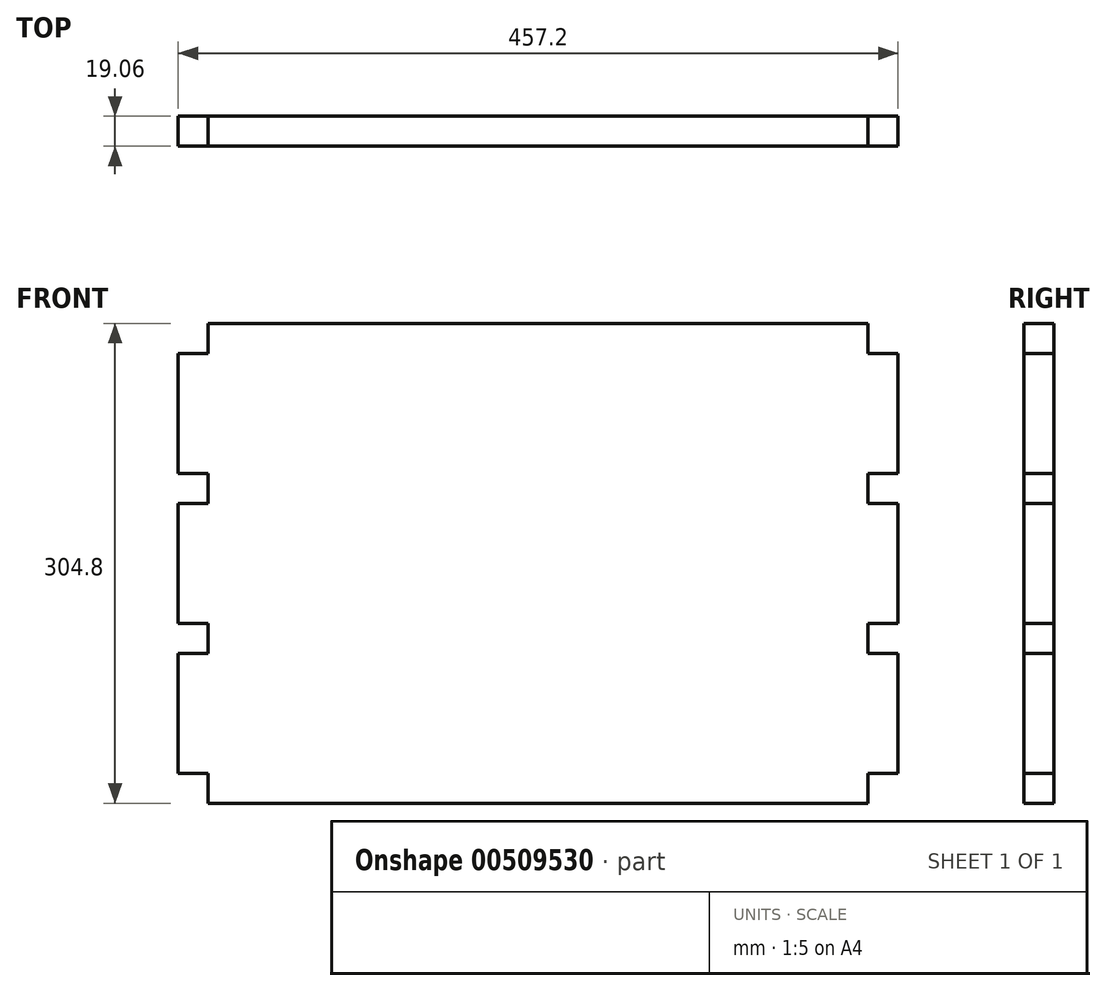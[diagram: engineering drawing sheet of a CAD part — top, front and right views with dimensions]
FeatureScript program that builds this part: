
annotation { "Feature Type Name" : "Feature", "Feature Type Description" : "" }
export const myFeature = defineFeature(function(context is Context, id is Id, definition is map)
    precondition{}
    {
        {
            var Q0;
            Q0=qCreatedBy(makeId("Front.planeOp"),FACE);
            var sketch = newSketch(context, id + "F0", { "sketchPlane" : qUnion([Q0])});
            skLineSegment(sketch, "E0.bottom", {"start": v(-228.6, 152.4) * mm, "end": v(228.6, 152.4) * mm});
            skLineSegment(sketch, "E0.top", {"start": v(-228.6, -152.4) * mm, "end": v(228.6, -152.4) * mm});
            skLineSegment(sketch, "E0.left", {"start": v(-228.6, 152.4) * mm, "end": v(-228.6, -152.4) * mm});
            skLineSegment(sketch, "E0.right", {"start": v(228.6, 152.4) * mm, "end": v(228.6, -152.4) * mm});
            skPoint(sketch, "E0.middle", {"position": v(0, 0) * mm});
            skSolve(sketch);
        }
        {
            var Q0;
            Q0=makeQuery(id+"F0.imprint","IMPRINT",FACE,{"disambiguationData":[TD([[makeQuery(id+"F0.imprint","IMPRINT",EDGE,{"derivedFrom":sQuery(id+"F0.wireOp",EDGE,"E0.bottom")}),-1.0]])]});
            extrude(context, id + "F1", {"entities" : qUnion([Q0]), "endBound" : BoundingType.SYMMETRIC, "depth" : 19.05 * mm, "offsetDistance" : 25.4 * mm});
        }
        {
            var Q0;
            Q0=makeQuery(id+"F1.opExtrude","SWEPT_FACE",FACE,{"disambiguationData":[OSD([sQuery(id+"F0.wireOp",EDGE,"E0.left")])]});
            var sketch = newSketch(context, id + "F2", { "sketchPlane" : qUnion([Q0])});
            skLineSegment(sketch, "E1", {"start": v(9.53, 133.35) * mm, "end": v(-9.52, 133.35) * mm});
            skLineSegment(sketch, "E2", {"start": v(-9.53, 133.35) * mm, "end": v(-9.53, 57.15) * mm});
            skLineSegment(sketch, "E3", {"start": v(-9.53, 57.15) * mm, "end": v(9.53, 57.15) * mm});
            skLineSegment(sketch, "E4", {"start": v(9.53, 57.15) * mm, "end": v(9.53, 133.35) * mm});
            skLineSegment(sketch, "E5", {"start": v(9.53, 38.1) * mm, "end": v(-9.53, 38.1) * mm});
            skLineSegment(sketch, "E6", {"start": v(-9.53, 38.1) * mm, "end": v(-9.53, -38.1) * mm});
            skLineSegment(sketch, "E7", {"start": v(-9.53, -38.1) * mm, "end": v(9.52, -38.1) * mm});
            skLineSegment(sketch, "E8", {"start": v(9.52, -38.1) * mm, "end": v(9.52, 38.1) * mm});
            skLineSegment(sketch, "E9", {"start": v(9.53, -57.15) * mm, "end": v(-9.52, -57.15) * mm});
            skLineSegment(sketch, "E10", {"start": v(-9.53, -57.15) * mm, "end": v(-9.53, -133.35) * mm});
            skLineSegment(sketch, "E11", {"start": v(-9.52, -133.35) * mm, "end": v(9.53, -133.35) * mm});
            skLineSegment(sketch, "E12", {"start": v(9.53, -133.35) * mm, "end": v(9.53, -57.15) * mm});
            skSolve(sketch);
        }
        {
            var Q0;
            {var subQ0=sQuery(id+"F2.wireOp",EDGE,"E1");Q0=makeQuery(id+"F2.imprint","IMPRINT",FACE,{"disambiguationData":[TD([[makeQuery(id+"F2.imprint","IMPRINT",EDGE,{"derivedFrom":subQ0}),-1.0]])]});}
            var Q1;
            {var subQ0=sQuery(id+"F2.wireOp",EDGE,"E3");Q1=makeQuery(id+"F2.imprint","IMPRINT",FACE,{"disambiguationData":[TD([[makeQuery(id+"F2.imprint","IMPRINT",EDGE,{"derivedFrom":subQ0}),-1.0]])]});}
            var Q2;
            {var subQ0=sQuery(id+"F2.wireOp",EDGE,"E7");Q2=makeQuery(id+"F2.imprint","IMPRINT",FACE,{"disambiguationData":[TD([[makeQuery(id+"F2.imprint","IMPRINT",EDGE,{"derivedFrom":subQ0}),-1.0]])]});}
            var Q3;
            {var subQ0=sQuery(id+"F2.wireOp",EDGE,"E11");Q3=makeQuery(id+"F2.imprint","IMPRINT",FACE,{"disambiguationData":[TD([[makeQuery(id+"F2.imprint","IMPRINT",EDGE,{"derivedFrom":subQ0}),-1.0]])]});}
            extrude(context, id + "F3", {"entities" : qUnion([Q0, Q1, Q2, Q3]), "operationType" : NewBodyOperationType.REMOVE, "oppositeDirection" : true, "depth" : 19.05 * mm, "offsetDistance" : 25.4 * mm});
        }
        {
            var Q0;
            Q0=makeQuery(id+"F1.opExtrude","SWEPT_FACE",FACE,{"disambiguationData":[OSD([sQuery(id+"F0.wireOp",EDGE,"E0.right")])]});
            var sketch = newSketch(context, id + "F4", { "sketchPlane" : qUnion([Q0])});
            skLineSegment(sketch, "E13.bottom", {"start": v(-9.53, -133.35) * mm, "end": v(9.53, -133.35) * mm});
            skLineSegment(sketch, "E13.top", {"start": v(-9.53, -57.15) * mm, "end": v(9.53, -57.15) * mm});
            skLineSegment(sketch, "E13.left", {"start": v(-9.53, -133.35) * mm, "end": v(-9.53, -57.15) * mm});
            skLineSegment(sketch, "E13.right", {"start": v(9.53, -133.35) * mm, "end": v(9.53, -57.15) * mm});
            skLineSegment(sketch, "E14.0.1.0", {"start": v(-9.53, -38.1) * mm, "end": v(-9.53, 38.1) * mm});
            skLineSegment(sketch, "E14.0.1.1", {"start": v(-9.53, 38.1) * mm, "end": v(9.53, 38.1) * mm});
            skLineSegment(sketch, "E14.0.1.2", {"start": v(9.53, -38.1) * mm, "end": v(9.53, 38.1) * mm});
            skLineSegment(sketch, "E14.0.1.3", {"start": v(-9.53, -38.1) * mm, "end": v(9.53, -38.1) * mm});
            skLineSegment(sketch, "E14.0.2.0", {"start": v(-9.53, 57.15) * mm, "end": v(-9.53, 133.35) * mm});
            skLineSegment(sketch, "E14.0.2.1", {"start": v(-9.53, 133.35) * mm, "end": v(9.53, 133.35) * mm});
            skLineSegment(sketch, "E14.0.2.2", {"start": v(9.53, 57.15) * mm, "end": v(9.53, 133.35) * mm});
            skLineSegment(sketch, "E14.0.2.3", {"start": v(-9.53, 57.15) * mm, "end": v(9.53, 57.15) * mm});
            skLineSegment(sketch, "E14.direction1", {"start": v(-9.52, -133.35) * mm, "end": v(15.88, -133.35) * mm, "construction": true});
            skLineSegment(sketch, "E14.direction2", {"start": v(-9.53, -133.35) * mm, "end": v(-9.53, -38.1) * mm, "construction": true});
            skSolve(sketch);
        }
        {
            var Q0;
            {var subQ0=sQuery(id+"F4.wireOp",EDGE,"E14.0.2.1");Q0=makeQuery(id+"F4.imprint","IMPRINT",FACE,{"disambiguationData":[TD([[makeQuery(id+"F4.imprint","IMPRINT",EDGE,{"derivedFrom":subQ0}),1.0]])]});}
            var Q1;
            {var subQ0=sQuery(id+"F4.wireOp",EDGE,"E14.0.1.1");Q1=makeQuery(id+"F4.imprint","IMPRINT",FACE,{"disambiguationData":[TD([[makeQuery(id+"F4.imprint","IMPRINT",EDGE,{"derivedFrom":subQ0}),1.0]])]});}
            var Q2;
            {var subQ0=sQuery(id+"F4.wireOp",EDGE,"E13.top");Q2=makeQuery(id+"F4.imprint","IMPRINT",FACE,{"disambiguationData":[TD([[makeQuery(id+"F4.imprint","IMPRINT",EDGE,{"derivedFrom":subQ0}),1.0]])]});}
            var Q3;
            {var subQ0=sQuery(id+"F4.wireOp",EDGE,"E13.bottom");Q3=makeQuery(id+"F4.imprint","IMPRINT",FACE,{"disambiguationData":[TD([[makeQuery(id+"F4.imprint","IMPRINT",EDGE,{"derivedFrom":subQ0}),-1.0]])]});}
            extrude(context, id + "F5", {"entities" : qUnion([Q0, Q1, Q2, Q3]), "operationType" : NewBodyOperationType.REMOVE, "oppositeDirection" : true, "depth" : 19.05 * mm, "offsetDistance" : 25.4 * mm});
        }
    });
